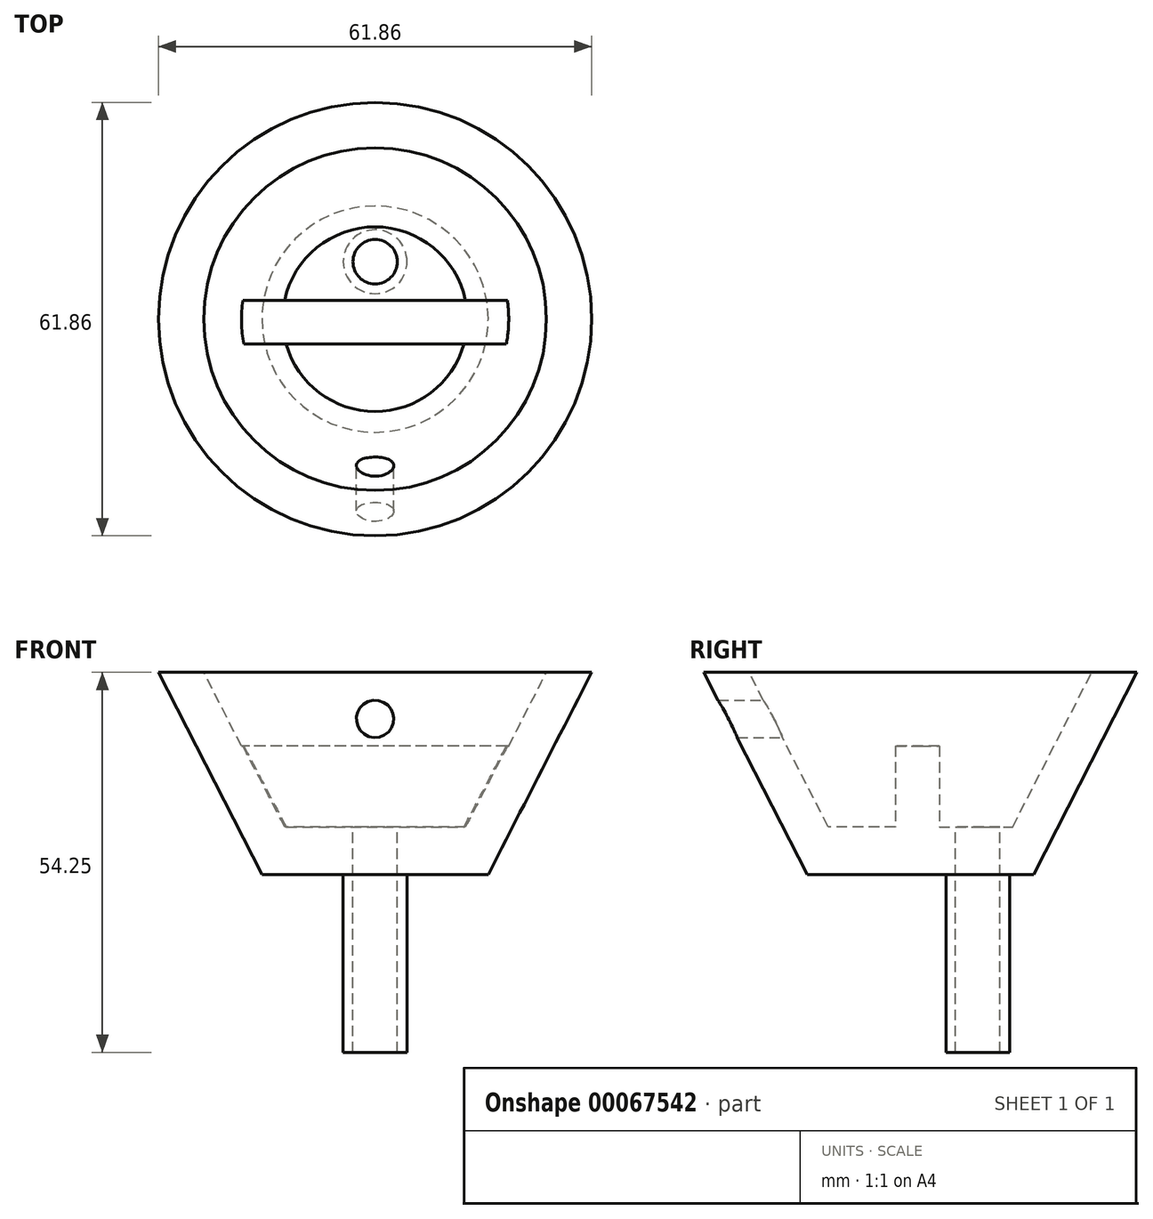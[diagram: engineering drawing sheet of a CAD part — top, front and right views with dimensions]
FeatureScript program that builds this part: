
annotation { "Feature Type Name" : "Feature", "Feature Type Description" : "" }
export const myFeature = defineFeature(function(context is Context, id is Id, definition is map)
    precondition{}
    {
        {
            var Q0;
            Q0=qCreatedBy(makeId("Front.planeOp"),FACE);
            var sketch = newSketch(context, id + "F0", { "sketchPlane" : qUnion([Q0])});
            skLineSegment(sketch, "E0", {"start": v(0, 0) * mm, "end": v(16.16, 0) * mm});
            skLineSegment(sketch, "E1", {"start": v(16.16, 0) * mm, "end": v(30.93, 28.85) * mm});
            skLineSegment(sketch, "E2", {"start": v(30.93, 28.85) * mm, "end": v(24.46, 28.85) * mm});
            skLineSegment(sketch, "E3", {"start": v(24.46, 28.85) * mm, "end": v(13.18, 6.8) * mm});
            skLineSegment(sketch, "E4", {"start": v(13.18, 6.8) * mm, "end": v(0, 6.8) * mm});
            skLineSegment(sketch, "E5", {"start": v(0, 6.8) * mm, "end": v(0, 0) * mm});
            skLineSegment(sketch, "E6", {"start": v(0, 39) * mm, "end": v(0, -26.54) * mm, "construction": true});
            skSolve(sketch);
        }
        {
            var Q0;
            Q0 = qSketchRegion(id + "F0", true);
            var Q1;
            Q1=sQuery(id+"F0.wireOp",EDGE,"E6");
            revolve(context, id + "F1", {"entities" : qUnion([Q0]), "axis" : qUnion([Q1]), "revolveType" : RevolveType.FULL});
        }
        {
            var Q0;
            Q0=qCreatedBy(makeId("Right.planeOp"),FACE);
            var sketch = newSketch(context, id + "F2", { "sketchPlane" : qUnion([Q0])});
            skLineSegment(sketch, "E7", {"start": v(-3.58, 0) * mm, "end": v(-3.58, 18.33) * mm});
            skLineSegment(sketch, "E8", {"start": v(-3.58, 18.33) * mm, "end": v(2.68, 18.33) * mm});
            skLineSegment(sketch, "E9", {"start": v(2.68, 18.33) * mm, "end": v(2.68, 0) * mm});
            skLineSegment(sketch, "E10", {"start": v(2.68, 0) * mm, "end": v(-3.58, 0) * mm});
            skSolve(sketch);
        }
        {
            var Q0;
            Q0=makeQuery(id+"F2.imprint","IMPRINT",FACE,{"disambiguationData":[TD([[makeQuery(id+"F2.imprint","IMPRINT",EDGE,{"derivedFrom":sQuery(id+"F2.wireOp",EDGE,"E7")}),-1.0]])]});
            extrude(context, id + "F3", {"entities" : qUnion([Q0]), "operationType" : NewBodyOperationType.ADD, "endBound" : BoundingType.UP_TO_NEXT, "depth" : 25.4 * mm, "hasSecondDirection" : true, "secondDirectionBound" : SecondDirectionBoundingType.THROUGH_ALL, "secondDirectionOppositeDirection" : true, "secondDirectionDepth" : 12.7 * mm});
        }
        {
            var Q0;
            Q0=makeQuery(id+"F3.boolean.opBoolean","SPLIT",FACE,{"disambiguationData":[TD([makeQuery(id+"F3.opExtrude","SWEPT_FACE",FACE,{"disambiguationData":[OSD([sQuery(id+"F2.wireOp",EDGE,"E9")])]})])],"derivedFrom":makeQuery(id+"F1.opRevolve","SWEPT_FACE",FACE,{"disambiguationData":[OSD([sQuery(id+"F0.wireOp",EDGE,"E4")])]})});
            var sketch = newSketch(context, id + "F4", { "sketchPlane" : qUnion([Q0])});
            skCircle(sketch, "E11", {"center": v(0, 8.2) * mm, "radius": 3.17 * mm});
            skSolve(sketch);
        }
        {
            var Q0;
            Q0 = qSketchRegion(id + "F4", true);
            extrude(context, id + "F5", {"entities" : qUnion([Q0]), "operationType" : NewBodyOperationType.REMOVE, "oppositeDirection" : true, "depth" : 25.4 * mm});
        }
        {
            var Q0;
            Q0=makeQuery(id+"F1.opRevolve","SWEPT_FACE",FACE,{"disambiguationData":[OSD([sQuery(id+"F0.wireOp",EDGE,"E0")])]});
            var sketch = newSketch(context, id + "F6", { "sketchPlane" : qUnion([Q0])});
            skCircle(sketch, "E12", {"center": v(0, -8.2) * mm, "radius": 4.56 * mm});
            skSolve(sketch);
        }
        {
            var Q0;
            Q0=makeQuery(id+"F6.imprint","IMPRINT",FACE,{"disambiguationData":[TD([[makeQuery(id+"F6.imprint","IMPRINT",EDGE,{"derivedFrom":sQuery(id+"F6.wireOp",EDGE,"E12")}),1.0]])]});
            extrude(context, id + "F7", {"entities" : qUnion([Q0]), "operationType" : NewBodyOperationType.ADD, "depth" : 25.4 * mm});
        }
        {
            var Q0;
            Q0=qCreatedBy(makeId("Front.planeOp"),FACE);
            var sketch = newSketch(context, id + "F8", { "sketchPlane" : qUnion([Q0])});
            skCircle(sketch, "E13", {"center": v(0, 22.2) * mm, "radius": 2.67 * mm});
            skSolve(sketch);
        }
        {
            var Q0;
            Q0 = qSketchRegion(id + "F8", true);
            extrude(context, id + "F9", {"entities" : qUnion([Q0]), "operationType" : NewBodyOperationType.REMOVE, "endBound" : BoundingType.THROUGH_ALL, "depth" : 25.4 * mm});
        }
    });
